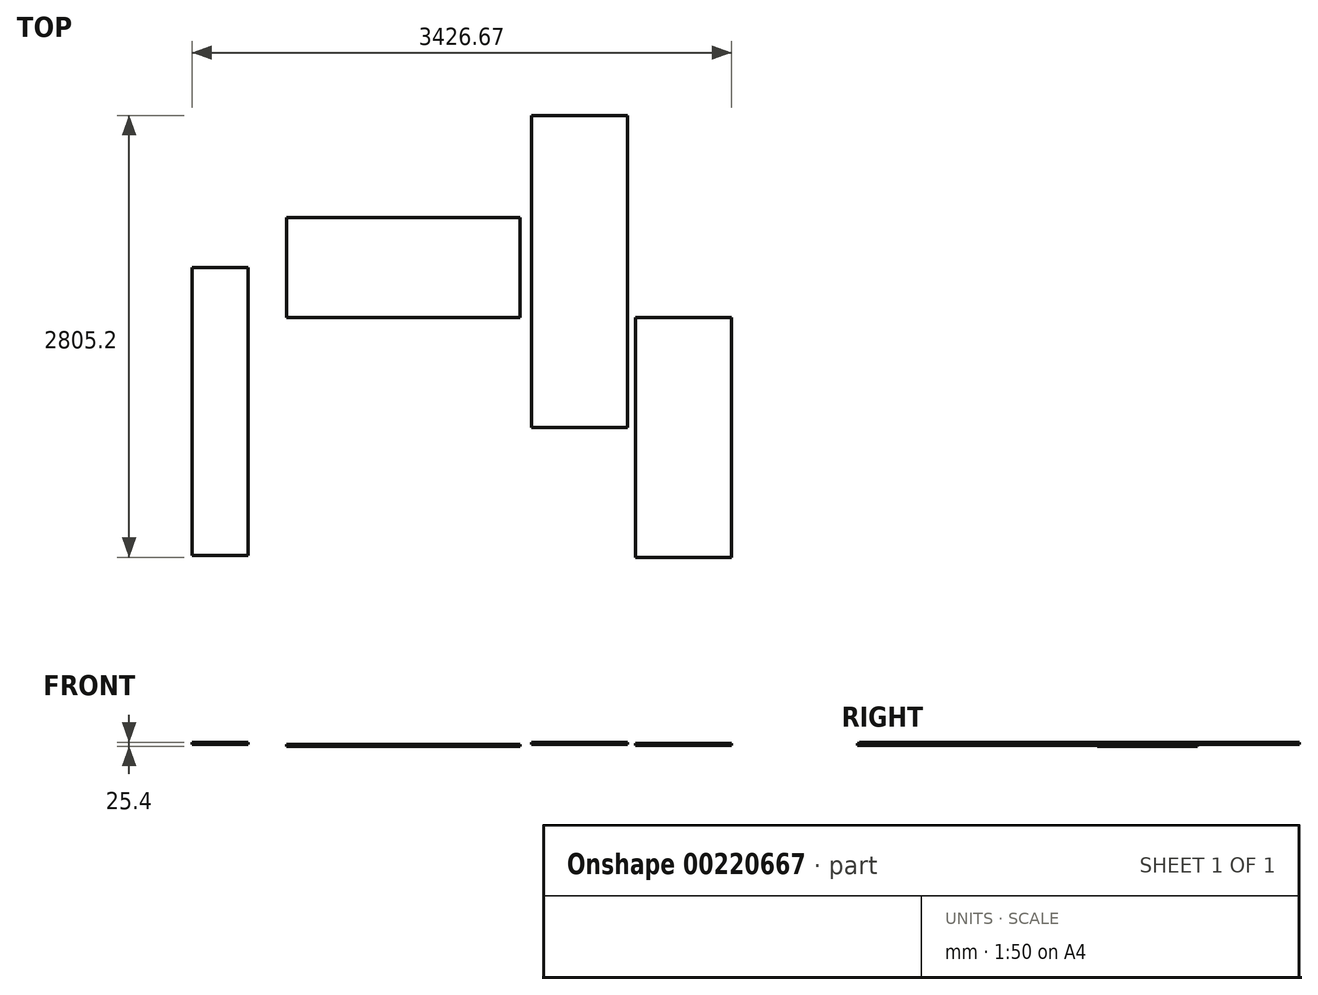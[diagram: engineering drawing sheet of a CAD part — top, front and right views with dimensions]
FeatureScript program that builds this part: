
annotation { "Feature Type Name" : "Feature", "Feature Type Description" : "" }
export const myFeature = defineFeature(function(context is Context, id is Id, definition is map)
    precondition{}
    {
        {
            var Q0;
            Q0=qCreatedBy(makeId("Front.planeOp"),FACE);
            var sketch = newSketch(context, id + "F0", { "sketchPlane" : qUnion([Q0])});
            skLineSegment(sketch, "E0.bottom", {"start": v(742.95, -6.35) * mm, "end": v(-742.95, -6.35) * mm});
            skLineSegment(sketch, "E0.top", {"start": v(742.95, 6.35) * mm, "end": v(-742.95, 6.35) * mm});
            skLineSegment(sketch, "E0.left", {"start": v(742.95, -6.35) * mm, "end": v(742.95, 6.35) * mm});
            skLineSegment(sketch, "E0.right", {"start": v(-742.95, -6.35) * mm, "end": v(-742.95, 6.35) * mm});
            skPoint(sketch, "E0.middle", {"position": v(0, 0) * mm});
            skSolve(sketch);
        }
        {
            var Q0;
            Q0 = qSketchRegion(id + "F0", true);
            extrude(context, id + "F1", {"entities" : qUnion([Q0]), "endBound" : BoundingType.SYMMETRIC, "depth" : 635 * mm});
        }
        {
            var Q0;
            Q0=makeQuery(id+"F1.opExtrude","SWEPT_FACE",FACE,{"disambiguationData":[OSD([sQuery(id+"F0.wireOp",EDGE,"E0.top")])]});
            var sketch = newSketch(context, id + "F2", { "sketchPlane" : qUnion([Q0])});
            skLineSegment(sketch, "E1.bottom", {"start": v(813.26, -1017.5) * mm, "end": v(1422.86, -1017.5) * mm});
            skLineSegment(sketch, "E1.top", {"start": v(813.26, 963.7) * mm, "end": v(1422.86, 963.7) * mm});
            skLineSegment(sketch, "E1.left", {"start": v(813.26, -1017.5) * mm, "end": v(813.26, 963.7) * mm});
            skLineSegment(sketch, "E1.right", {"start": v(1422.86, -1017.5) * mm, "end": v(1422.86, 963.7) * mm});
            skSolve(sketch);
        }
        {
            var Q0;
            Q0 = qSketchRegion(id + "F2", true);
            extrude(context, id + "F3", {"entities" : qUnion([Q0]), "depth" : 12.7 * mm});
        }
        {
            var Q0;
            Q0=makeQuery(id+"F1.opExtrude","SWEPT_FACE",FACE,{"disambiguationData":[OSD([sQuery(id+"F0.wireOp",EDGE,"E0.top")])]});
            var sketch = newSketch(context, id + "F4", { "sketchPlane" : qUnion([Q0])});
            skPoint(sketch, "E2.firstSnap0", {"position": v(-742.95, 0) * mm});
            skLineSegment(sketch, "E2.bottom", {"start": v(-1341.14, 0) * mm, "end": v(-985.54, 0) * mm});
            skLineSegment(sketch, "E2.top", {"start": v(-1341.14, -1828.8) * mm, "end": v(-985.54, -1828.8) * mm});
            skLineSegment(sketch, "E2.left", {"start": v(-1341.14, 0) * mm, "end": v(-1341.14, -1828.8) * mm});
            skLineSegment(sketch, "E2.right", {"start": v(-985.54, 0) * mm, "end": v(-985.54, -1828.8) * mm});
            skSolve(sketch);
        }
        {
            var Q0;
            Q0 = qSketchRegion(id + "F4", true);
            extrude(context, id + "F5", {"entities" : qUnion([Q0]), "depth" : 12.7 * mm});
        }
        {
            var Q0;
            Q0=makeQuery(id+"F1.opExtrude","CAP_FACE",FACE,{"disambiguationData":[OSD([sQuery(id+"F0.wireOp",EDGE,"E0.bottom"),sQuery(id+"F0.wireOp",EDGE,"E0.top"),sQuery(id+"F0.wireOp",EDGE,"E0.left"),sQuery(id+"F0.wireOp",EDGE,"E0.right")])],"isStart":false});
            var sketch = newSketch(context, id + "F6", { "sketchPlane" : qUnion([Q0])});
            skLineSegment(sketch, "E3.bottom", {"start": v(1475.93, 12.7) * mm, "end": v(2085.53, 12.7) * mm});
            skLineSegment(sketch, "E3.top", {"start": v(1475.93, 0) * mm, "end": v(2085.53, 0) * mm});
            skLineSegment(sketch, "E3.left", {"start": v(1475.93, 12.7) * mm, "end": v(1475.93, 0) * mm});
            skLineSegment(sketch, "E3.right", {"start": v(2085.53, 12.7) * mm, "end": v(2085.53, 0) * mm});
            skSolve(sketch);
        }
        {
            var Q0;
            Q0 = qSketchRegion(id + "F6", true);
            extrude(context, id + "F7", {"entities" : qUnion([Q0]), "depth" : 1524 * mm});
        }
    });
